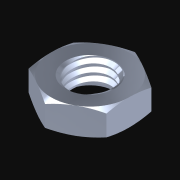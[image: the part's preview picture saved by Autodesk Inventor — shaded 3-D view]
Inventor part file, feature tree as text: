
AUTODESK INVENTOR PART (.ipt)
format: ipt  version: 2021 (Build 250183000, 183)  size: 248,320 bytes
history: native  units: in
note: dims shown in document units (in); Inventor stores cm internally (conversion verified against a paired STEP export)
features: other x3, imported_body x1, sketch x1, extrude x1
ambient origin geometry x8: Origin, YZ Plane, XZ Plane, XY Plane, X Axis, Y Axis, Z Axis, Center Point
bodies: Body1 (feature_tree), Body2 (feature_tree)
feature tree (6):
  parser-record x1  (decoder bookkeeping rows leaked as tree rows — omitted from the tree; the rows remain in map.json)
  other  "90695A0371"
  imported_body  "Base1"
  sketch  "Sketch1"  dims[d0=0.002in d1=0.1063in d2=0.0in]
  other  "Srf1"
  extrude  "ExtrusionSrf1"  Depth=0.1063in TaperAngle=0.0deg
